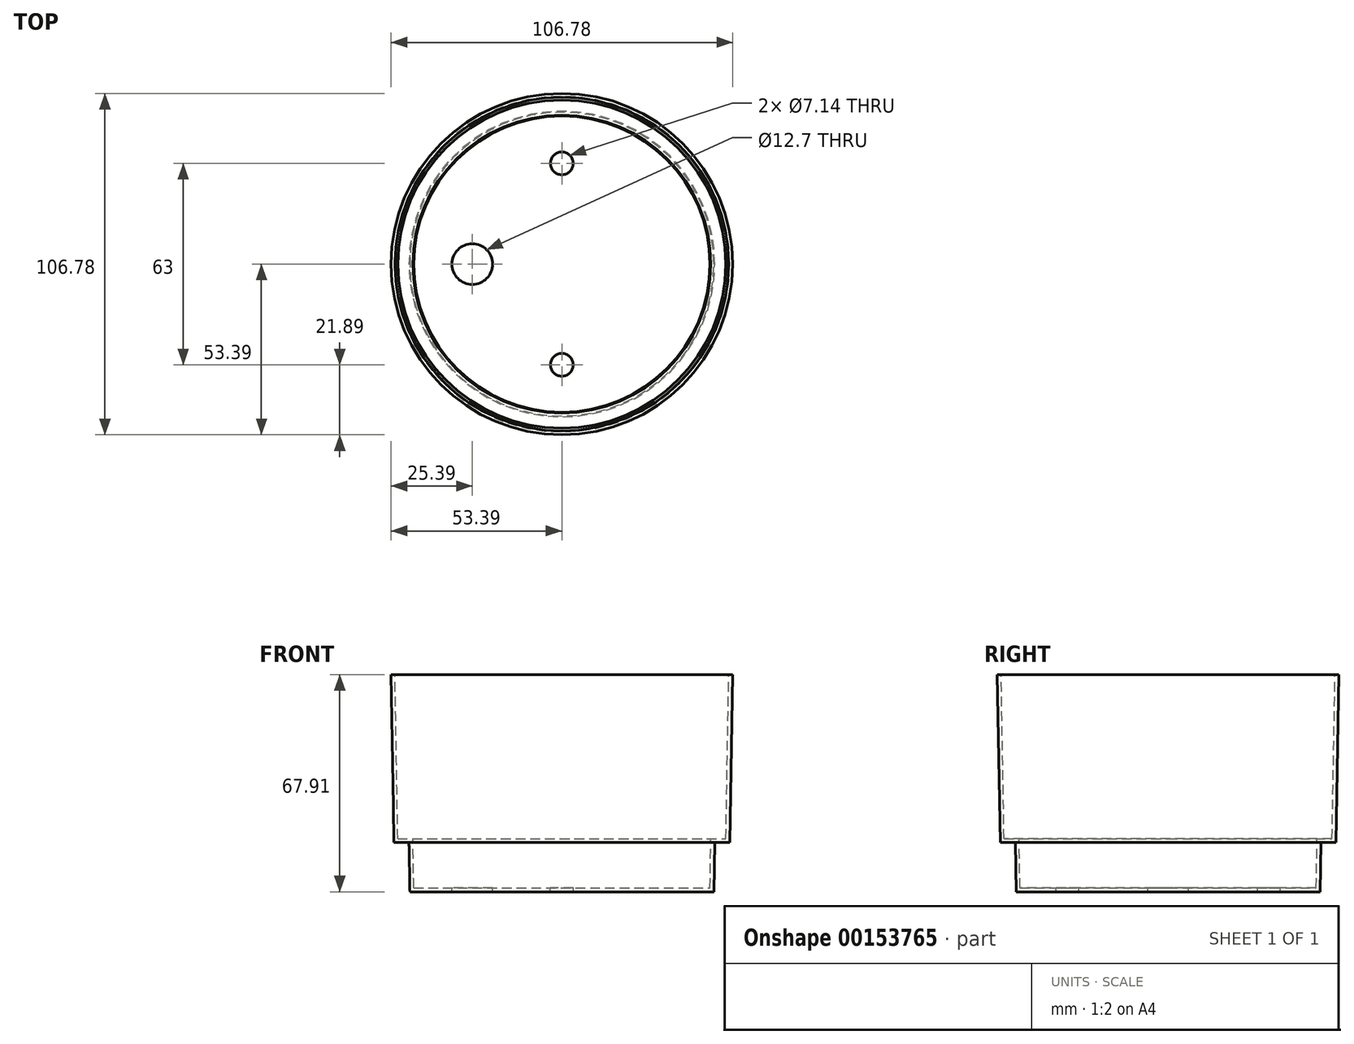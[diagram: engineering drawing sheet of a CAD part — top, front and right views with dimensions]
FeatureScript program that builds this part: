
annotation { "Feature Type Name" : "Feature", "Feature Type Description" : "" }
export const myFeature = defineFeature(function(context is Context, id is Id, definition is map)
    precondition{}
    {
        {
            var Q0;
            Q0=qCreatedBy(makeId("Front.planeOp"),FACE);
            var sketch = newSketch(context, id + "F0", { "sketchPlane" : qUnion([Q0])});
            skLineSegment(sketch, "E0", {"start": v(0, 1.22) * mm, "end": v(-46.31, 1.22) * mm});
            skLineSegment(sketch, "E1", {"start": v(-46.31, 1.22) * mm, "end": v(-46.58, 16.62) * mm});
            skLineSegment(sketch, "E2", {"start": v(-47.5, 0) * mm, "end": v(0, 0) * mm});
            skLineSegment(sketch, "E3", {"start": v(0, 0) * mm, "end": v(0, 1.22) * mm});
            skLineSegment(sketch, "E4", {"start": v(-46.58, 16.62) * mm, "end": v(-51.28, 16.62) * mm});
            skLineSegment(sketch, "E5", {"start": v(-51.28, 16.62) * mm, "end": v(-52.18, 67.91) * mm});
            skLineSegment(sketch, "E6.0", {"start": v(-52.47, 15.4) * mm, "end": v(-53.39, 67.9) * mm});
            skLineSegment(sketch, "E6.1", {"start": v(-47.77, 15.4) * mm, "end": v(-52.47, 15.4) * mm});
            skLineSegment(sketch, "E6.2", {"start": v(-47.5, 0) * mm, "end": v(-47.77, 15.4) * mm});
            skLineSegment(sketch, "E7", {"start": v(-53.39, 67.9) * mm, "end": v(-52.18, 67.91) * mm});
            skLineSegment(sketch, "E8", {"start": v(0, 1.22) * mm, "end": v(0, 40.3) * mm, "construction": true});
            skSolve(sketch);
        }
        {
            var Q0;
            Q0 = qSketchRegion(id + "F0", true);
            var Q1;
            Q1=sQuery(id+"F0.wireOp",EDGE,"E8");
            revolve(context, id + "F1", {"entities" : qUnion([Q0]), "axis" : qUnion([Q1]), "revolveType" : RevolveType.FULL});
        }
        {
            var Q0;
            Q0=makeQuery(id+"F1.opRevolve","SWEPT_FACE",FACE,{"disambiguationData":[OSD([sQuery(id+"F0.wireOp",EDGE,"E0")])]});
            var sketch = newSketch(context, id + "F2", { "sketchPlane" : qUnion([Q0])});
            skCircle(sketch, "E9", {"center": v(0, 31.5) * mm, "radius": 3.57 * mm});
            skCircle(sketch, "E10", {"center": v(0, -31.5) * mm, "radius": 3.57 * mm});
            skCircle(sketch, "E11", {"center": v(-28, 0) * mm, "radius": 6.35 * mm});
            skSolve(sketch);
        }
        {
            var Q0;
            Q0 = qSketchRegion(id + "F2", true);
            extrude(context, id + "F3", {"entities" : qUnion([Q0]), "operationType" : NewBodyOperationType.REMOVE, "endBound" : BoundingType.UP_TO_NEXT, "oppositeDirection" : true, "depth" : 25.4 * mm});
        }
    });
